# Revit family: Mixing_Valve-Emergency-Bradley_Corp-Navigator_EFX8-S19-2000EFX
name_source: partatom
category: Pipe Accessories
revit_build: Autodesk Revit Architecture 2012 (Build: 20110916_2132(x64)
units: mm (PartAtom-declared; Revit-internal decimal feet)

## types (1)
- EFX 8
    ADA Compliant = No
    Assembly Code = D2090800
    Description = Emergency Fixture Thermostatic Mixing Valve (EFX 8)
    Industry Standards = ANSI Z358.1-2004
    Manufacturer = Bradley Corporation
    MasterFormat Number = 22 45 36
    MasterFormat Title = Emergency Fixture Water-Tempering Equipment
    Material = Brass
    Maximum Inlet Temperature = 180°F (82°C)
    Maximum Operating Pressure = 125.00 psi
    Model = S19-2000EFX
    Modeling Code = ABO090623JRRL1200ABC090703TAS1122
    NPT = 1"
    NPT Radius = 0"
    Nut Material = Metal - Bradley Corp - Light Bronze
    OmniClass Code = 23.65.55.14.24
    OmniClass Title = Mixing Valves for Liquid Services
    Percentage of Recycled Content = 0
    Product Tech Data URL - English = http://bradleycorp.com
    Recommended Inlet Temperature = 120°F (49°C) - 140°F (60°C)
    Set Point = 85°F (29°C)
    Specifications URL = http://www.bradleycorp.com
    Temperature Range = Std. 65°F (18°C) to 95°F (35°C)
    URL = http://www.bradleycorp.com
    Valve Material = Metal - Bradley Corp - Bronze
    Version = 2.0

## geometry (parser evidence)
native form markers: Blend x16, Sweep x2
no freeform markers — native parametric forms only
